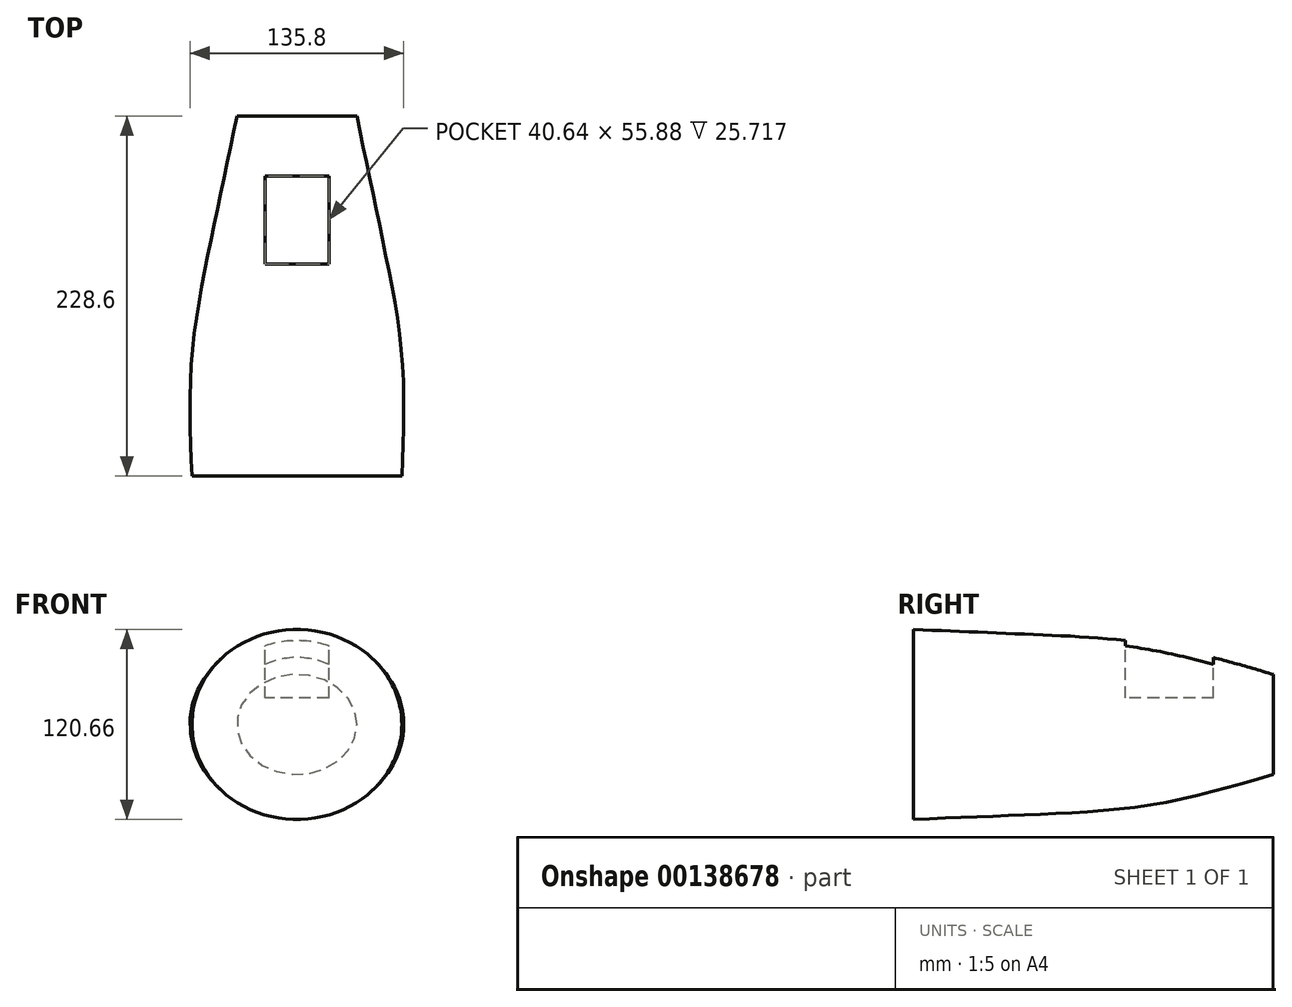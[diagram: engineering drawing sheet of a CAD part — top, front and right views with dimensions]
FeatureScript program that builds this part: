
annotation { "Feature Type Name" : "Feature", "Feature Type Description" : "" }
export const myFeature = defineFeature(function(context is Context, id is Id, definition is map)
    precondition{}
    {
        {
            var Q0;
            Q0=qCreatedBy(makeId("Front.planeOp"),FACE);
            var sketch = newSketch(context, id + "F0", { "sketchPlane" : qUnion([Q0])});
            skEllipse(sketch, "E0", {"center": v(0, 0) * mm, "majorRadius": 38.1 * mm, "minorRadius": 31.75 * mm, "majorAxis": v(1, 0)});
            skSolve(sketch);
        }
        {
            var Q0;
            Q0=qCreatedBy(makeId("Front.planeOp"),FACE);
            cPlane(context, id + "F1", {"entities" : qUnion([Q0]), "cplaneType" : CPlaneType.OFFSET, "offset" : 76.2 * mm, "width" : 152.4 * mm, "height" : 152.4 * mm});
        }
        {
            var Q0;
            Q0=qCreatedBy(id+"F1.planeOp",FACE);
            var sketch = newSketch(context, id + "F2", { "sketchPlane" : qUnion([Q0])});
            skPoint(sketch, "E1.0", {"position": v(0, 0) * mm});
            skEllipse(sketch, "E2", {"center": v(0, 0) * mm, "majorRadius": 53.98 * mm, "minorRadius": 50.8 * mm, "majorAxis": v(1, 0)});
            skSolve(sketch);
        }
        {
            var Q0;
            Q0=qCreatedBy(makeId("Front.planeOp"),FACE);
            cPlane(context, id + "F3", {"entities" : qUnion([Q0]), "cplaneType" : CPlaneType.OFFSET, "offset" : 152.4 * mm, "width" : 152.4 * mm, "height" : 152.4 * mm});
        }
        {
            var Q0;
            Q0=qCreatedBy(id+"F3.planeOp",FACE);
            var sketch = newSketch(context, id + "F4", { "sketchPlane" : qUnion([Q0])});
            skPoint(sketch, "E3.0", {"position": v(0, 0) * mm});
            skEllipse(sketch, "E4", {"center": v(0, 0) * mm, "majorRadius": 66.68 * mm, "minorRadius": 57.15 * mm, "majorAxis": v(-1, 0)});
            skSolve(sketch);
        }
        {
            var Q0;
            Q0=qCreatedBy(makeId("Front.planeOp"),FACE);
            cPlane(context, id + "F5", {"entities" : qUnion([Q0]), "cplaneType" : CPlaneType.OFFSET, "offset" : 228.6 * mm, "width" : 152.4 * mm, "height" : 152.4 * mm});
        }
        {
            var Q0;
            Q0=qCreatedBy(id+"F5.planeOp",FACE);
            var sketch = newSketch(context, id + "F6", { "sketchPlane" : qUnion([Q0])});
            skPoint(sketch, "E5.0", {"position": v(0, 0) * mm});
            skEllipse(sketch, "E6", {"center": v(0, 0) * mm, "majorRadius": 66.68 * mm, "minorRadius": 60.33 * mm, "majorAxis": v(-1, 0)});
            skSolve(sketch);
        }
        {
            var Q0;
            Q0=makeQuery(id+"F0.imprint","IMPRINT",FACE,{"disambiguationData":[TD([[makeQuery(id+"F0.imprint","IMPRINT",EDGE,{"derivedFrom":sQuery(id+"F0.wireOp",EDGE,"E0")}),1.0]])]});
            var Q1;
            Q1=makeQuery(id+"F2.imprint","IMPRINT",FACE,{"disambiguationData":[TD([[makeQuery(id+"F2.imprint","IMPRINT",EDGE,{"derivedFrom":sQuery(id+"F2.wireOp",EDGE,"E2")}),1.0]])]});
            var Q2;
            Q2=makeQuery(id+"F4.imprint","IMPRINT",FACE,{"disambiguationData":[TD([[makeQuery(id+"F4.imprint","IMPRINT",EDGE,{"derivedFrom":sQuery(id+"F4.wireOp",EDGE,"E4")}),1.0]])]});
            var Q3;
            Q3=makeQuery(id+"F6.imprint","IMPRINT",FACE,{"disambiguationData":[TD([[makeQuery(id+"F6.imprint","IMPRINT",EDGE,{"derivedFrom":sQuery(id+"F6.wireOp",EDGE,"E6")}),1.0]])]});
            loft(context, id + "F7", {"sheetProfilesArray" : [{ "sheetProfileEntities" : qUnion([Q0]) }, { "sheetProfileEntities" : qUnion([Q1]) }, { "sheetProfileEntities" : qUnion([Q2]) }, { "sheetProfileEntities" : qUnion([Q3]) }]});
        }
        {
            var Q0;
            Q0=qCreatedBy(makeId("Top.planeOp"),FACE);
            cPlane(context, id + "F8", {"entities" : qUnion([Q0]), "cplaneType" : CPlaneType.OFFSET, "offset" : 101.6 * mm, "width" : 152.4 * mm, "height" : 152.4 * mm});
        }
        {
            var Q0;
            Q0=qCreatedBy(id+"F8.planeOp",FACE);
            var sketch = newSketch(context, id + "F9", { "sketchPlane" : qUnion([Q0])});
            skFitSpline(sketch, "E7.0", {"points": [v(38.1, 0) * mm, v(12.7, 0) * mm, v(-12.7, 0) * mm, v(-38.1, 0) * mm]});
            skFitSpline(sketch, "E8.0", {"points": [v(66.68, -228.6) * mm, v(22.23, -228.6) * mm, v(-22.22, -228.6) * mm, v(-66.67, -228.6) * mm]});
            skLineSegment(sketch, "E9", {"start": v(0, 0) * mm, "end": v(0, -228.6) * mm});
            skLineSegment(sketch, "E10.bottom", {"start": v(20.32, -38.1) * mm, "end": v(-20.32, -38.1) * mm});
            skLineSegment(sketch, "E10.top", {"start": v(20.32, -93.98) * mm, "end": v(-20.32, -93.98) * mm});
            skLineSegment(sketch, "E10.left", {"start": v(20.32, -38.1) * mm, "end": v(20.32, -93.98) * mm});
            skLineSegment(sketch, "E10.right", {"start": v(-20.32, -38.1) * mm, "end": v(-20.32, -93.98) * mm});
            skSolve(sketch);
        }
        {
            var Q0;
            {var subQ5=sQuery(id+"F9.wireOp",EDGE,"E10.left");Q0=makeQuery(id+"F9.imprint","IMPRINT",FACE,{"disambiguationData":[TD([[makeQuery(id+"F9.imprint","IMPRINT",EDGE,{"derivedFrom":subQ5}),-1.0]])]});}
            var Q1;
            {var subQ5=sQuery(id+"F9.wireOp",EDGE,"E10.right");Q1=makeQuery(id+"F9.imprint","IMPRINT",FACE,{"disambiguationData":[TD([[makeQuery(id+"F9.imprint","IMPRINT",EDGE,{"derivedFrom":subQ5}),1.0]])]});}
            extrude(context, id + "F10", {"entities" : qUnion([Q0, Q1]), "operationType" : NewBodyOperationType.REMOVE, "oppositeDirection" : true, "depth" : 84.84 * mm});
        }
    });
